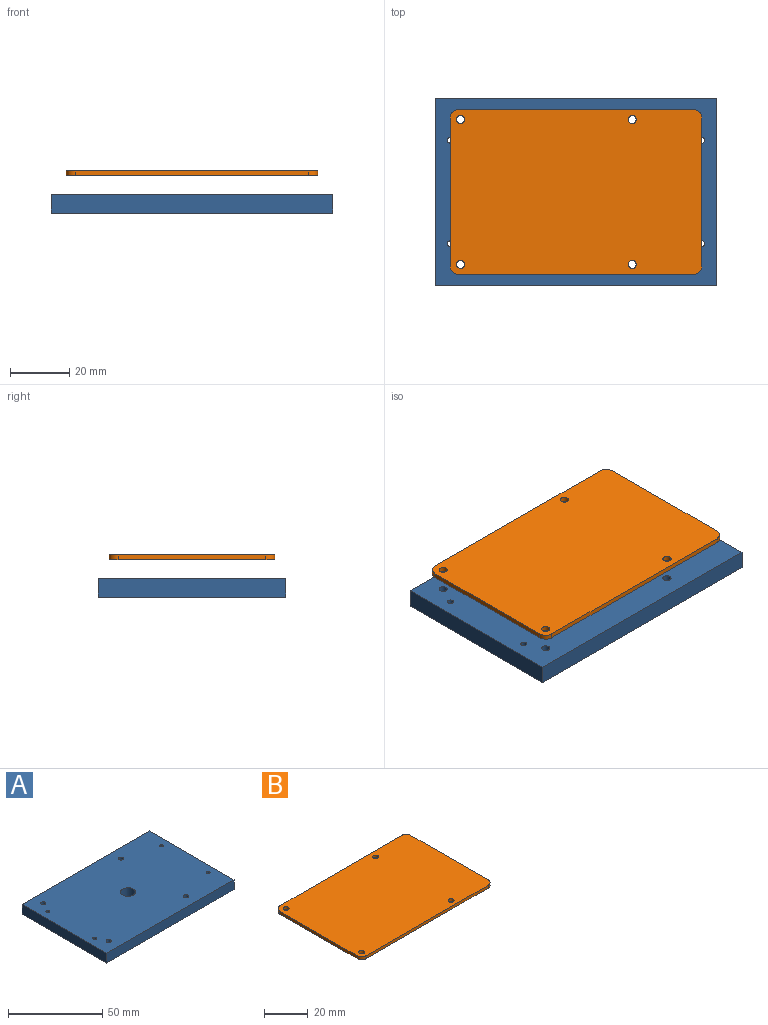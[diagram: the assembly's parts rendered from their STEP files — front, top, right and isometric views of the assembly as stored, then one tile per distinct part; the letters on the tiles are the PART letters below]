
ASSEMBLY  parts=2 mates=1
PART A: 15 faces, bbox 95.3x63.5x6.4 mm
  f0: plane 95.25x6.35mm, normal (0,1,0), area 604.8mm2, adj f1,f3,f4,f5
  f1: plane 63.5x6.35mm, normal (-1,0,0), area 403.2mm2, adj f0,f2,f4,f5
  f2: plane 95.25x6.35mm, normal (0,-1,0), area 604.8mm2, adj f1,f3,f4,f5
  f3: plane 63.5x6.35mm, normal (1,0,0), area 403.2mm2, adj f0,f2,f4,f5
  f4: plane 95.25x63.5mm, normal (0,0,-1), area 5962.6mm2, adj f0,f1,f2,f3,f6,f7,f8,f9
  f5: plane 95.25x63.5mm, normal (0,0,1), area 5962.6mm2, adj f0,f1,f2,f3,f6,f7,f8,f9
  f6: cylinder r=1.38mm len=6.35mm, axis (0,0,1), area 54.9mm2, adj f4,f5
  f7: cylinder r=1.38mm len=6.35mm, axis (0,0,1), area 54.9mm2, adj f4,f5
  f8: cylinder r=1.38mm len=6.35mm, axis (0,0,1), area 54.9mm2, adj f4,f5
  f9: cylinder r=1.38mm len=6.35mm, axis (0,0,1), area 54.9mm2, adj f4,f5
  f10: cylinder r=1mm len=6.35mm, axis (0,0,1), area 39.9mm2, adj f4,f5
  f11: cylinder r=1mm len=6.35mm, axis (0,0,1), area 39.9mm2, adj f4,f5
  f12: cylinder r=1mm len=6.35mm, axis (0,0,1), area 39.9mm2, adj f4,f5
  f13: cylinder r=1mm len=6.35mm, axis (0,0,1), area 39.9mm2, adj f4,f5
  f14: cylinder r=3.97mm len=7.94mm, axis (0,0,1), area 158.3mm2, adj f4,f5
PART B: 14 faces, bbox 85x56x1.6 mm
  f0: plane 79x1.6mm, normal (0,1,0), area 126.4mm2, adj f1,f7,f8,f9
  f1: cylinder r=3mm len=3mm, axis (0,0,1), area 7.5mm2, adj f0,f2,f8,f9
  f2: plane 50x1.6mm, normal (-1,0,0), area 80mm2, adj f1,f3,f8,f9
  f3: cylinder r=3mm len=3mm, axis (0,0,1), area 7.5mm2, adj f2,f4,f8,f9
  f4: plane 79x1.6mm, normal (0,-1,0), area 126.4mm2, adj f3,f5,f8,f9
  f5: cylinder r=3mm len=3mm, axis (0,0,1), area 7.5mm2, adj f4,f6,f8,f9
  f6: plane 50x1.6mm, normal (1,0,0), area 80mm2, adj f5,f7,f8,f9
  f7: cylinder r=3mm len=3mm, axis (0,0,1), area 7.5mm2, adj f0,f6,f8,f9
  f8: plane 85x56mm, normal (0,0,-1), area 4728.5mm2, adj f0,f1,f2,f3,f4,f5,f6,f7
  f9: plane 85x56mm, normal (0,0,1), area 4728.5mm2, adj f0,f1,f2,f3,f4,f5,f6,f7
  f10: cylinder r=1.38mm len=2.75mm, axis (0,0,1), area 13.8mm2, adj f8,f9
  f11: cylinder r=1.38mm len=2.75mm, axis (0,0,1), area 13.8mm2, adj f8,f9
  f12: cylinder r=1.38mm len=2.75mm, axis (0,0,1), area 13.8mm2, adj f8,f9
  f13: cylinder r=1.38mm len=2.75mm, axis (0,0,1), area 13.8mm2, adj f8,f9
PLACE A at identity fixed
PLACE B t=(0,0,7.95)mm
MATE fastened B.f10 <-> A.f6  axis (0,0,-1) through (-39,24.5,6.35)mm
